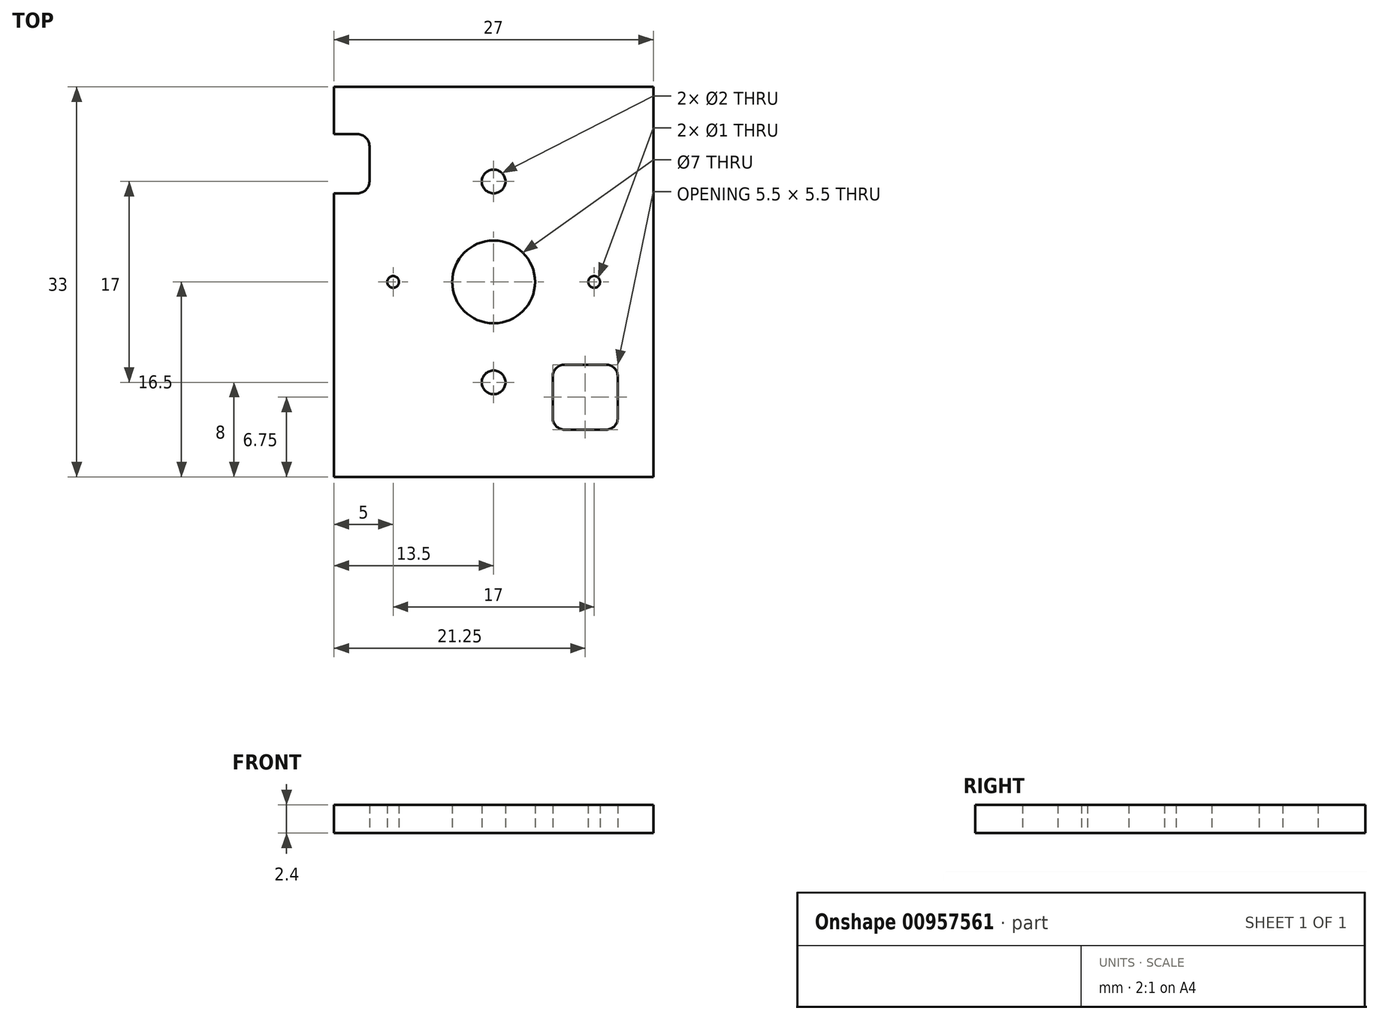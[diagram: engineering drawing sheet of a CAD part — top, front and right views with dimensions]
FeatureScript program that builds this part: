
annotation { "Feature Type Name" : "Feature", "Feature Type Description" : "" }
export const myFeature = defineFeature(function(context is Context, id is Id, definition is map)
    precondition{}
    {
        {
            var Q0;
            Q0=qCreatedBy(makeId("Top.planeOp"),FACE);
            var sketch = newSketch(context, id + "F0", { "sketchPlane" : qUnion([Q0])});
            skLineSegment(sketch, "E0.bottom", {"start": v(13.5, -16.5) * mm, "end": v(-13.5, -16.5) * mm});
            skLineSegment(sketch, "E0.top", {"start": v(13.5, 16.5) * mm, "end": v(-13.5, 16.5) * mm});
            skLineSegment(sketch, "E0.left", {"start": v(13.5, -16.5) * mm, "end": v(13.5, 16.5) * mm});
            skLineSegment(sketch, "E0.right", {"start": v(-13.5, -16.5) * mm, "end": v(-13.5, 16.5) * mm});
            skPoint(sketch, "E0.middle", {"position": v(0, 0) * mm});
            skLineSegment(sketch, "E1", {"start": v(-13.5, 16.5) * mm, "end": v(-13.5, 12.5) * mm});
            skLineSegment(sketch, "E2", {"start": v(-13.5, 12.5) * mm, "end": v(-11.5, 12.5) * mm});
            skLineSegment(sketch, "E3", {"start": v(-10.5, 11.5) * mm, "end": v(-10.5, 8.5) * mm});
            skLineSegment(sketch, "E4", {"start": v(-11.5, 7.5) * mm, "end": v(-13.5, 7.5) * mm});
            skCircle(sketch, "E5", {"center": v(0, 0) * mm, "radius": 3.5 * mm});
            skLineSegment(sketch, "E6", {"start": v(0, 0) * mm, "end": v(8.5, 0) * mm});
            skLineSegment(sketch, "E7", {"start": v(0, 0) * mm, "end": v(0, 8.5) * mm});
            skCircle(sketch, "E8", {"center": v(8.5, 0) * mm, "radius": 0.5 * mm});
            skCircle(sketch, "E9", {"center": v(0, 8.5) * mm, "radius": 1 * mm});
            skCircle(sketch, "E10.1.0", {"center": v(0, -8.5) * mm, "radius": 1 * mm});
            skCircle(sketch, "E11.1.0", {"center": v(-8.5, 0) * mm, "radius": 0.5 * mm});
            skPoint(sketch, "E12.visualSharp", {"position": v(-10.5, 12.5) * mm});
            skArc(sketch, "E12.filletArc", {"start": v(-10.5, 11.5) * mm, "mid": v(-10.8, 12.2) * mm, "end": v(-11.5, 12.5) * mm});
            skPoint(sketch, "E13.visualSharp", {"position": v(-10.5, 7.5) * mm});
            skArc(sketch, "E13.filletArc", {"start": v(-11.5, 7.5) * mm, "mid": v(-10.8, 7.8) * mm, "end": v(-10.5, 8.5) * mm});
            skLineSegment(sketch, "E14.bottom", {"start": v(9.5, -12.5) * mm, "end": v(6, -12.5) * mm});
            skLineSegment(sketch, "E14.top", {"start": v(9.5, -7) * mm, "end": v(6, -7) * mm});
            skLineSegment(sketch, "E14.left", {"start": v(10.5, -11.5) * mm, "end": v(10.5, -8) * mm});
            skLineSegment(sketch, "E14.right", {"start": v(5, -11.5) * mm, "end": v(5, -8) * mm});
            skPoint(sketch, "E15.visualSharp", {"position": v(5, -7) * mm});
            skArc(sketch, "E15.filletArc", {"start": v(6, -7) * mm, "mid": v(5.3, -7.3) * mm, "end": v(5, -8) * mm});
            skPoint(sketch, "E16.visualSharp", {"position": v(10.5, -7) * mm});
            skArc(sketch, "E16.filletArc", {"start": v(10.5, -8) * mm, "mid": v(10.2, -7.3) * mm, "end": v(9.5, -7) * mm});
            skPoint(sketch, "E17.visualSharp", {"position": v(5, -12.5) * mm});
            skArc(sketch, "E17.filletArc", {"start": v(5, -11.5) * mm, "mid": v(5.3, -12.2) * mm, "end": v(6, -12.5) * mm});
            skPoint(sketch, "E18.visualSharp", {"position": v(10.5, -12.5) * mm});
            skArc(sketch, "E18.filletArc", {"start": v(9.5, -12.5) * mm, "mid": v(10.2, -12.2) * mm, "end": v(10.5, -11.5) * mm});
            skSolve(sketch);
        }
        {
            var Q0;
            {var subQ1=sQuery(id+"F0.wireOp",EDGE,"E0.bottom");Q0=makeQuery(id+"F0.imprint","IMPRINT",FACE,{"disambiguationData":[TD([[makeQuery(id+"F0.imprint","IMPRINT",EDGE,{"derivedFrom":subQ1}),-1.0]])]});}
            extrude(context, id + "F1", {"entities" : qUnion([Q0]), "depth" : 2.4 * mm, "offsetDistance" : 25 * mm});
        }
    });
